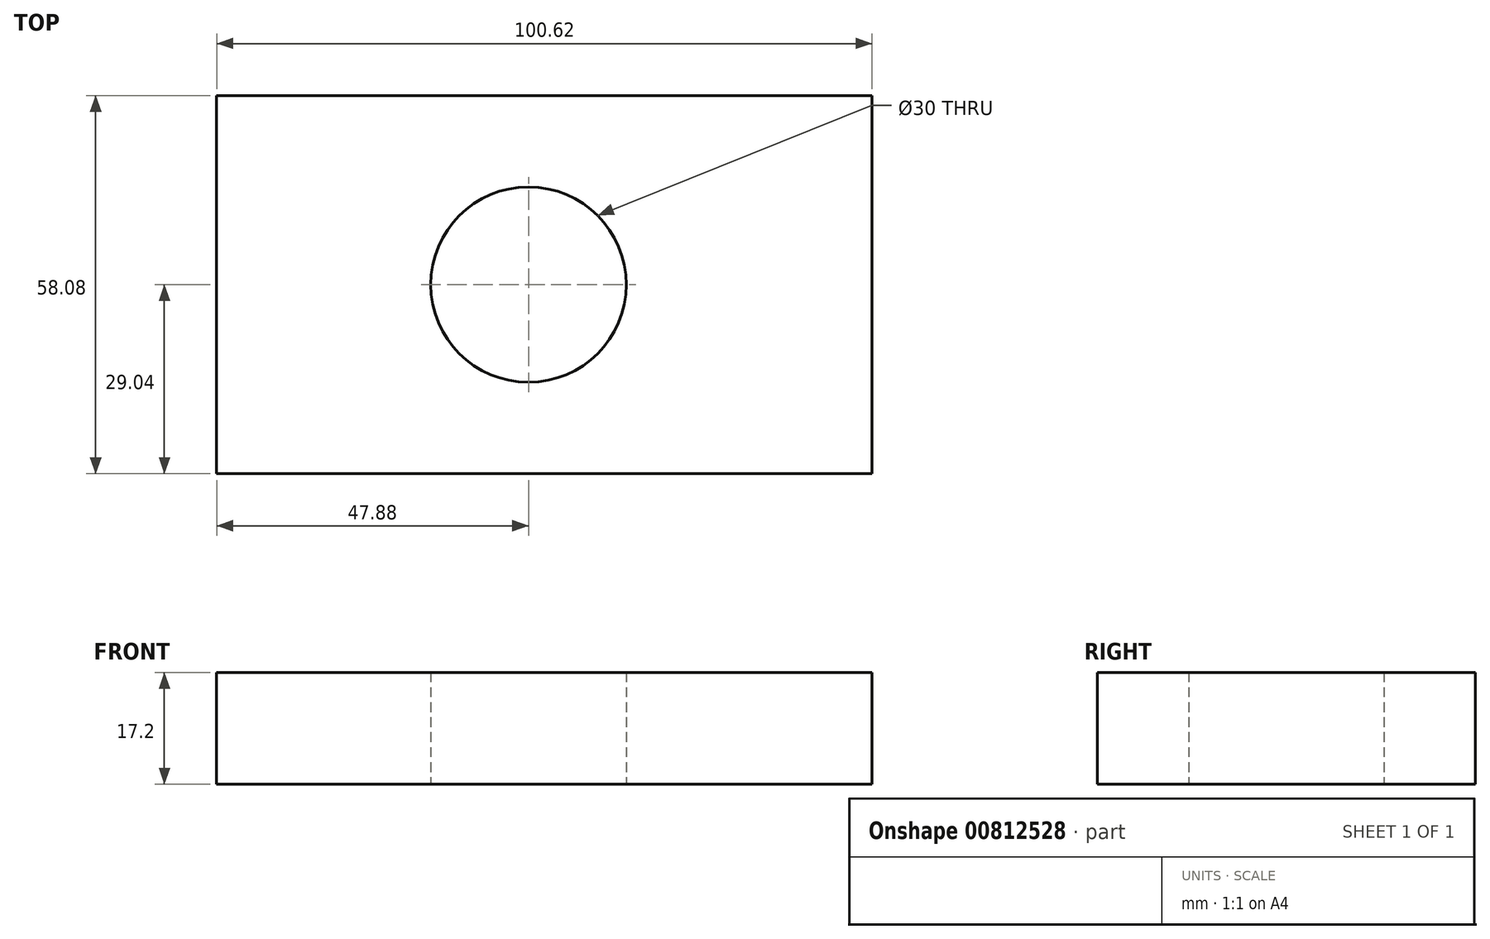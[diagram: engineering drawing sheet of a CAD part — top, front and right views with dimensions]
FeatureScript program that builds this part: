
annotation { "Feature Type Name" : "Feature", "Feature Type Description" : "" }
export const myFeature = defineFeature(function(context is Context, id is Id, definition is map)
    precondition{}
    {
        {
            var Q0;
            Q0=qCreatedBy(makeId("Top.planeOp"),FACE);
            var sketch = newSketch(context, id + "F0", { "sketchPlane" : qUnion([Q0])});
            skLineSegment(sketch, "E0.bottom", {"start": v(-47.88, -29.04) * mm, "end": v(52.74, -29.04) * mm});
            skLineSegment(sketch, "E0.top", {"start": v(-47.88, 29.04) * mm, "end": v(52.74, 29.04) * mm});
            skLineSegment(sketch, "E0.left", {"start": v(-47.88, -29.04) * mm, "end": v(-47.88, 29.04) * mm});
            skLineSegment(sketch, "E0.right", {"start": v(52.74, -29.04) * mm, "end": v(52.74, 29.04) * mm});
            skPoint(sketch, "E0.middle", {"position": v(2.43, 0) * mm});
            skCircle(sketch, "E1", {"center": v(0, 0) * mm, "radius": 15 * mm});
            skSolve(sketch);
        }
        {
            var Q0;
            Q0=makeQuery(id+"F0.imprint","IMPRINT",FACE,{"disambiguationData":[TD([[makeQuery(id+"F0.imprint","IMPRINT",EDGE,{"derivedFrom":sQuery(id+"F0.wireOp",EDGE,"E0.bottom")}),1.0]])]});
            extrude(context, id + "F1", {"entities" : qUnion([Q0]), "depth" : 17.2 * mm, "offsetDistance" : 25 * mm});
        }
    });
